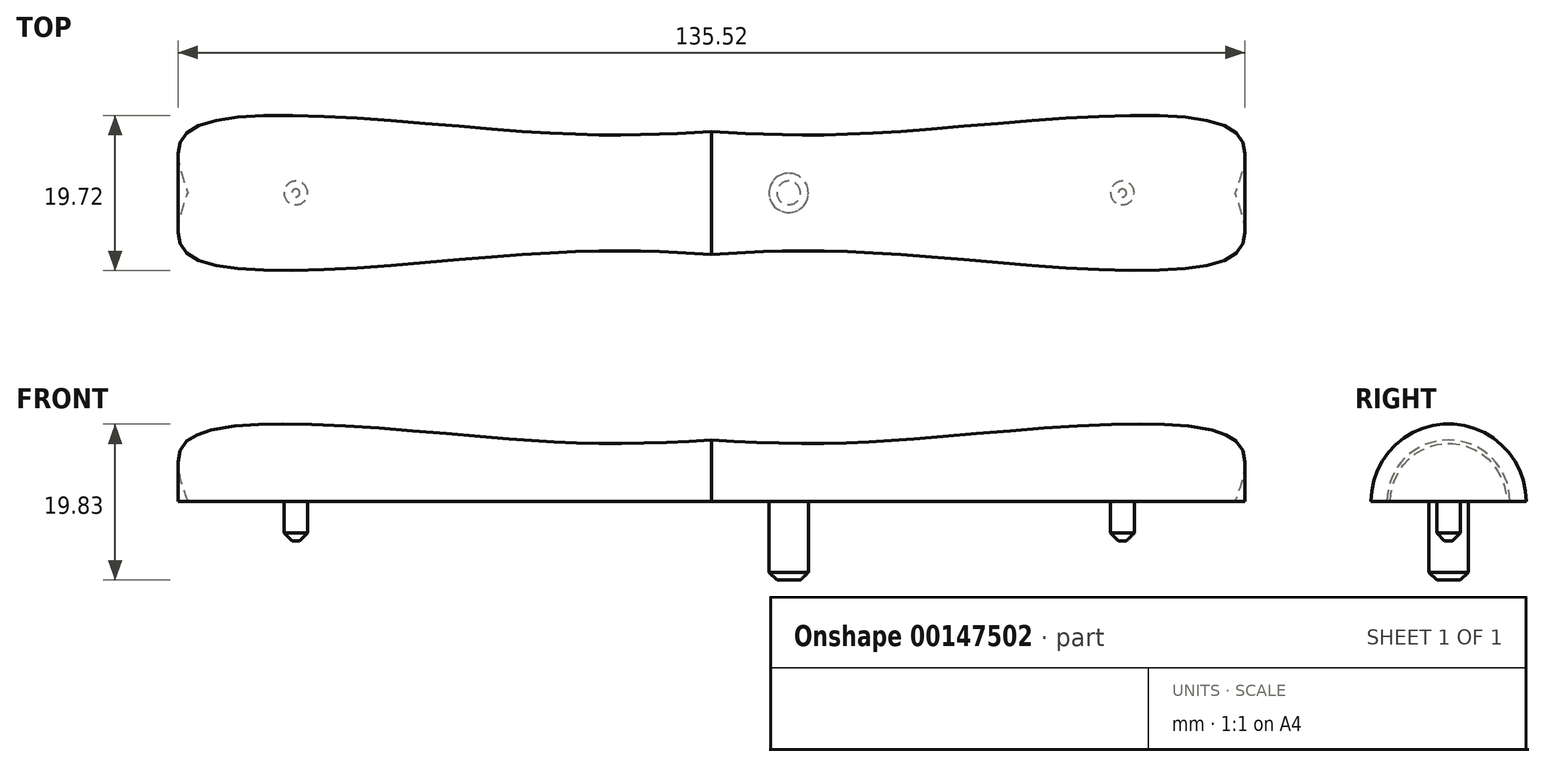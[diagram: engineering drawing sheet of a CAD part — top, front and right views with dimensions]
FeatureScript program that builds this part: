
annotation { "Feature Type Name" : "Feature", "Feature Type Description" : "" }
export const myFeature = defineFeature(function(context is Context, id is Id, definition is map)
    precondition{}
    {
        {
            var Q0;
            Q0=qCreatedBy(makeId("Top.planeOp"),FACE);
            var sketch = newSketch(context, id + "F0", { "sketchPlane" : qUnion([Q0])});
            skLineSegment(sketch, "E0", {"start": v(0, 50.53) * mm, "end": v(0, -41.05) * mm, "construction": true});
            skPoint(sketch, "E1", {"position": v(0, 7.8) * mm});
            skPoint(sketch, "E2.MirrorP", {"position": v(0, -7.8) * mm});
            skFitSpline(sketch, "E3", {"points": [v(0, 7.8) * mm, v(-66.5, 0) * mm], "startDerivative": vector(-70.78, 0) * mm, "endDerivative": vector(0, -23.4) * mm});
            skLineSegment(sketch, "E4", {"start": v(-66.5, 0) * mm, "end": v(-66.5, 7.8) * mm, "construction": true});
            skLineSegment(sketch, "E5", {"start": v(0, 7.8) * mm, "end": v(-66.5, 7.8) * mm, "construction": true});
            skFitSpline(sketch, "E6.MirrorCS", {"points": [v(0, -7.8) * mm, v(-66.5, 0) * mm], "startDerivative": vector(-70.78, 0) * mm, "endDerivative": vector(0, 23.4) * mm});
            skFitSpline(sketch, "E7.MirrorCS", {"points": [v(0, 7.8) * mm, v(66.5, 0) * mm], "startDerivative": vector(70.78, 0) * mm, "endDerivative": vector(0, -23.4) * mm});
            skFitSpline(sketch, "E8.MirrorCS", {"points": [v(0, -7.8) * mm, v(66.5, 0) * mm], "startDerivative": vector(70.78, 0) * mm, "endDerivative": vector(0, 23.4) * mm});
            skCircle(sketch, "E9.MirrorC", {"center": v(-53, 0) * mm, "radius": 1.5 * mm});
            skLineSegment(sketch, "E10", {"start": v(-66.5, 0) * mm, "end": v(66.5, 0) * mm, "construction": true});
            skCircle(sketch, "E11", {"center": v(51.5, 0) * mm, "radius": 1.5 * mm});
            skCircle(sketch, "E12", {"center": v(9.4, 0) * mm, "radius": 2.5 * mm});
            skLineSegment(sketch, "E13", {"start": v(-54.5, 0) * mm, "end": v(-54.5, 7.8) * mm, "construction": true});
            skSolve(sketch);
        }
        {
            var Q0;
            Q0=qCreatedBy(makeId("Top.planeOp"),FACE);
            var sketch = newSketch(context, id + "F1", { "sketchPlane" : qUnion([Q0])});
            skFitSpline(sketch, "E14.0", {"points": [v(0, 7.8) * mm, v(-23.6, 7.8) * mm, v(-66.5, 7.8) * mm, v(-66.5, 0) * mm]});
            skFitSpline(sketch, "E15.0", {"points": [v(0, 7.8) * mm, v(23.6, 7.8) * mm, v(66.5, 7.8) * mm, v(66.5, 0) * mm]});
            skLineSegment(sketch, "E16", {"start": v(-66.5, 0) * mm, "end": v(66.5, 0) * mm});
            skPoint(sketch, "E17.0.end.orphan", {"position": v(-66.5, 0) * mm});
            skPoint(sketch, "E18.0.start.orphan", {"position": v(0, -7.8) * mm});
            skSolve(sketch);
        }
        {
            var Q0;
            Q0=makeQuery(id+"F1.imprint","IMPRINT",FACE,{"disambiguationData":[TD([[makeQuery(id+"F1.imprint","IMPRINT",EDGE,{"derivedFrom":sQuery(id+"F1.wireOp",EDGE,"E14.0")}),1.0]])]});
            var Q1;
            Q1=sQuery(id+"F1.wireOp",EDGE,"E16");
            revolve(context, id + "F2", {"surfaceOperationType" : NewSurfaceOperationType.NEW, "entities" : qUnion([Q0]), "axis" : qUnion([Q1]), "revolveType" : RevolveType.ONE_DIRECTION, "angle" : 180 * degree});
        }
        {
            var Q0;
            Q0=qCreatedBy(makeId("Top.planeOp"),FACE);
            var sketch = newSketch(context, id + "F3", { "sketchPlane" : qUnion([Q0])});
            skCircle(sketch, "E19", {"center": v(9.8, 0) * mm, "radius": 2.5 * mm});
            skCircle(sketch, "E20", {"center": v(52.2, 0) * mm, "radius": 1.5 * mm});
            skCircle(sketch, "E21", {"center": v(-52.8, 0) * mm, "radius": 1.5 * mm});
            skLineSegment(sketch, "E22", {"start": v(66.5, -16.09) * mm, "end": v(66.5, 18.48) * mm, "construction": true});
            skLineSegment(sketch, "E23", {"start": v(-66.5, -18.2) * mm, "end": v(-66.5, 13.95) * mm, "construction": true});
            skSolve(sketch);
        }
        {
            var Q0;
            Q0=makeQuery(id+"F3.imprint","IMPRINT",FACE,{"disambiguationData":[TD([[makeQuery(id+"F3.imprint","IMPRINT",EDGE,{"derivedFrom":sQuery(id+"F3.wireOp",EDGE,"E21")}),1.0]])]});
            var Q1;
            Q1=makeQuery(id+"F3.imprint","IMPRINT",FACE,{"disambiguationData":[TD([[makeQuery(id+"F3.imprint","IMPRINT",EDGE,{"derivedFrom":sQuery(id+"F3.wireOp",EDGE,"E20")}),1.0]])]});
            var Q2;
            Q2=sQuery(id+"F3.wireOp",EDGE,"E21");
            var Q3;
            Q3=sQuery(id+"F3.wireOp",EDGE,"E20");
            extrude(context, id + "F4", {"entities" : qUnion([Q0, Q1]), "operationType" : NewBodyOperationType.ADD, "surfaceEntities" : qUnion([Q2, Q3]), "oppositeDirection" : true, "depth" : 5 * mm, "offsetDistance" : 25 * mm});
        }
        {
            var Q0;
            Q0=makeQuery(id+"F3.imprint","IMPRINT",FACE,{"disambiguationData":[TD([[makeQuery(id+"F3.imprint","IMPRINT",EDGE,{"derivedFrom":sQuery(id+"F3.wireOp",EDGE,"E19")}),1.0]])]});
            var Q1;
            Q1=sQuery(id+"F3.wireOp",EDGE,"E19");
            extrude(context, id + "F5", {"entities" : qUnion([Q0]), "operationType" : NewBodyOperationType.ADD, "surfaceEntities" : qUnion([Q1]), "oppositeDirection" : true, "depth" : 10 * mm, "offsetDistance" : 25 * mm});
        }
        {
            var Q0;
            Q0=makeQuery(id+"F4.opExtrude","CAP_EDGE",EDGE,{"disambiguationData":[OSD([sQuery(id+"F3.wireOp",EDGE,"E21")])],"isStart":false});
            var Q1;
            Q1=makeQuery(id+"F5.opExtrude","CAP_EDGE",EDGE,{"disambiguationData":[OSD([sQuery(id+"F3.wireOp",EDGE,"E19")])],"isStart":false});
            var Q2;
            Q2=makeQuery(id+"F4.opExtrude","CAP_EDGE",EDGE,{"disambiguationData":[OSD([sQuery(id+"F3.wireOp",EDGE,"E20")])],"isStart":false});
            chamfer(context, id + "F6", {"entities" : qUnion([Q0, Q1, Q2]), "width" : 1 * mm, "tangentPropagation" : true});
        }
    });
